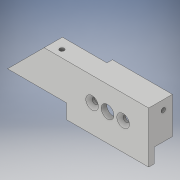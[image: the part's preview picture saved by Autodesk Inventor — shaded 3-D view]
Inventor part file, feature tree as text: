
AUTODESK INVENTOR PART (.ipt)
format: ipt  version: 2019 (Build 230136000, 136)  size: 235,008 bytes
history: native  units: in
note: dims shown in document units (in); Inventor stores cm internally (conversion verified against a paired STEP export)
features: sketch x11, extrude x7, hole x5
ambient origin geometry x8: Origin, YZ Plane, XZ Plane, XY Plane, X Axis, Y Axis, Z Axis, Center Point
bodies: Solid1 (feature_tree)
feature tree (23):
  extrude  "Extrusion1"  Depth=0.5118in
  extrude  "Extrusion2"  Depth=3.209in
  extrude  "Extrusion3"  Depth=0.315in
  extrude  "Extrusion4"  Depth=0.9843in
  extrude  "Extrusion5"  Depth=0.3937in
  hole  "Hole1"  [1 undecoded]
  hole  "Hole2"  [1 undecoded]
  hole  "Hole3"  [1 undecoded]
  hole  "Hole4"  [1 undecoded]
  extrude  "Extrusion6"  Depth=0.1181in
  extrude  "Extrusion7"  Depth=0.1181in
  hole  "Hole5"  [1 undecoded]
  sketch  "Sketch1"  dims[d0=3.2087in d1=0.5118in]
  sketch  "Sketch2"  dims[d2=1.1811in d3=0.0in d4=3.209in]
  sketch  "Sketch3"  dims[d5=0.315in d6=2.3228in]
  sketch  "Sketch4"  dims[d7=0.5906in d8=0.9843in]
  sketch  "Sketch6"  dims[d9=0.3937in d10=0.0in d11=0.8661in]
  sketch  "Sketch7"  dims[d12=1.7717in d13=0.5118in d14=0.0in]
  sketch  "Sketch9"  dims[d15=0.0787in d16=0.0in d17=0.2756in]
  sketch  "Sketch10"  dims[d18=0.1181in d19=0.0in d20=0.3346in]
  sketch  "Sketch11"  dims[d21=0.3346in]
  sketch  "Sketch12"  dims[d22=0.1339in d23=0.394in d24=0.2717in d25=0.25in d26=0.6181in d27=0.3937in d28=0.0in]
  sketch  "Sketch13"  dims[d32=0.1628in d33=0.394in d34=0.2717in d35=0.25in d36=0.6181in d37=0.2205in d38=0.8108in d40=0.1969in d43=0.0968in d44=0.236in d45=0.2717in d46=0.25in d47=0.6181in d48=0.3543in d49=0.8108in d52=0.0968in d53=0.236in d54=0.2717in d55=0.25in d56=0.6181in d57=0.3543in d58=0.8108in d62=0.0968in d63=0.236in d64=0.409in d65=0.25in d66=90.0deg d67=0.3937in d68=0.8108in d71=0.1181in d72=0.1181in d73=1.0in d74=0.0in d75=0.0489in d76=0.1575in d77=0.3937in d79=1.4567in d80=0.1181in d81=0.0in d82=0.315in d83=0.1969in d84=0.1969in d111=0.2087in d112=0.2756in d50=0.75in d51=0.8108in]
note: 5 required parameter values undecoded (feature->parameter linkage not recoverable at this tier; creation-order binding heuristic only, values carry confidence <= 0.55)
